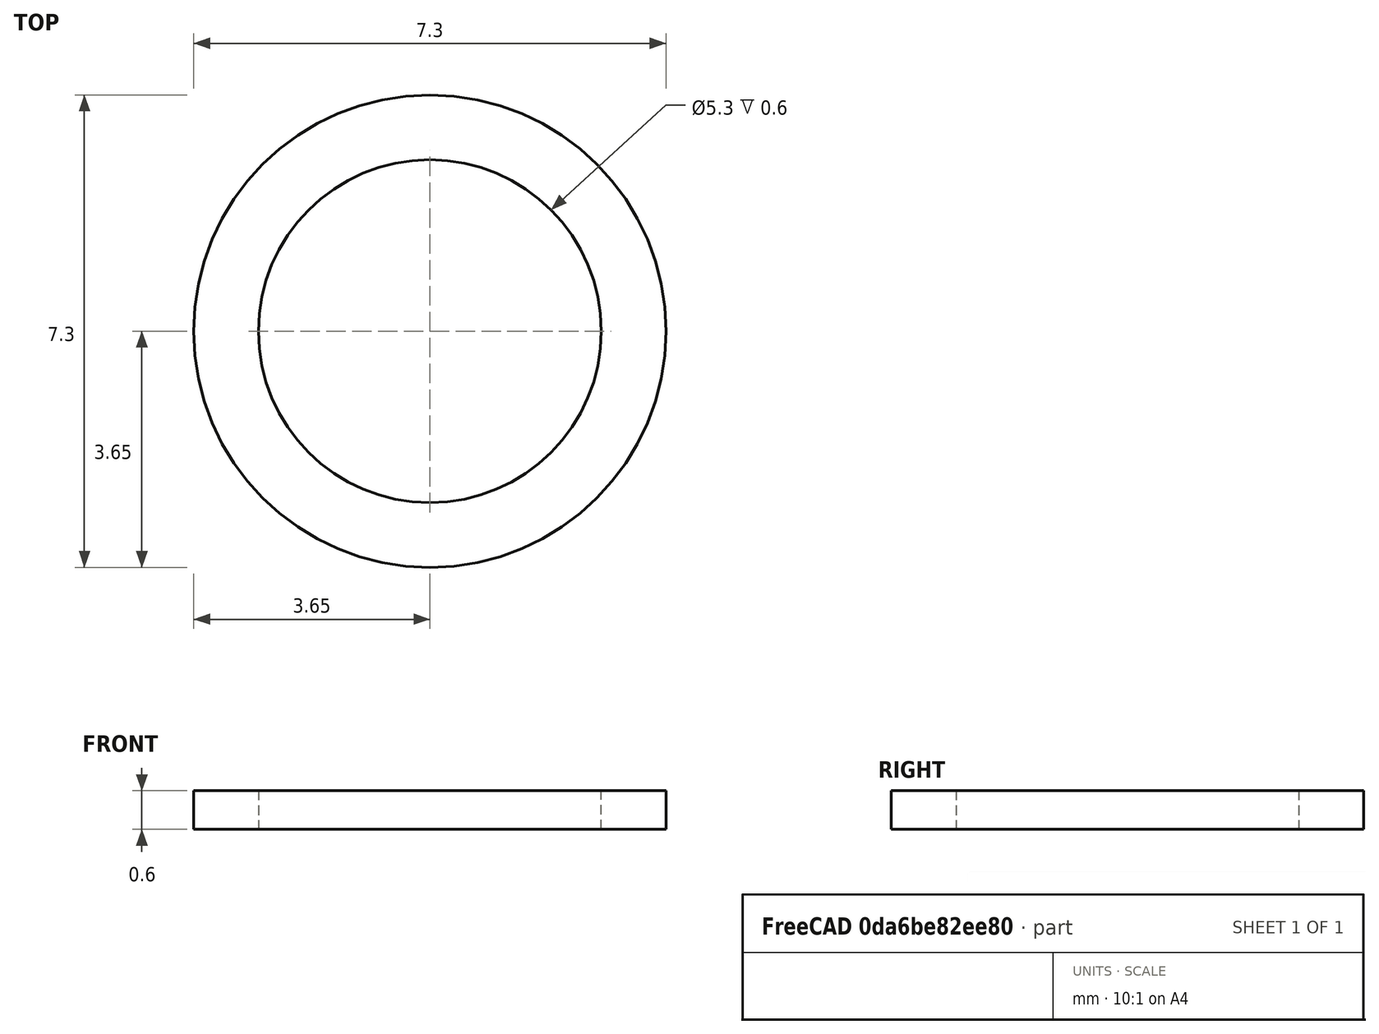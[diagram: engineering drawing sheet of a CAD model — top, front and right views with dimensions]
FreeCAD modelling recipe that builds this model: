
FCSTD DOCUMENT  (FreeCAD 0.20R29177 +426 (Git))
Label: IdlerPulleyWasher
License: All rights reserved
LicenseURL: http://en.wikipedia.org/wiki/All_rights_reserved
objects: Sketcher::SketchObject×1, PartDesign::Pad×1, PartDesign::Body×1
note: 4 computed .brp shape members not serialized (recipe doc carries the construction recipe); baked Part::Feature solids carry a one-line shape summary decoded from their .brp

FEATURE [Sketcher::SketchObject] Sketch
  FullyConstrained = true
  MapMode = 5
  Support = -> [XY_Plane]
  sketch-geometry (2):
    g0: Circle CenterX=0 CenterY=0 CenterZ=0 NormalX=0 NormalY=0 NormalZ=1 AngleXU=0 Radius=2.65
    g1: Circle CenterX=0 CenterY=0 CenterZ=0 NormalX=0 NormalY=0 NormalZ=1 AngleXU=0 Radius=3.65
  constraints (4):
    c: Coincident(g0,g-1)
    c: Coincident(g1,g0)
    c: Diameter(g0) = 5.3
    c: Diameter(g1) = 7.3
FEATURE [PartDesign::Pad] Pad
  Direction = (0,0,1)
  Length = 0.6
  Length2 = 10
  Profile = -> Sketch
  ReferenceAxis = -> Sketch [N_Axis]
  Type = 0
FEATURE [PartDesign::Body] Body
  Group = -> [Sketch,Pad]
  Origin = -> Origin
  Tip = -> Pad
